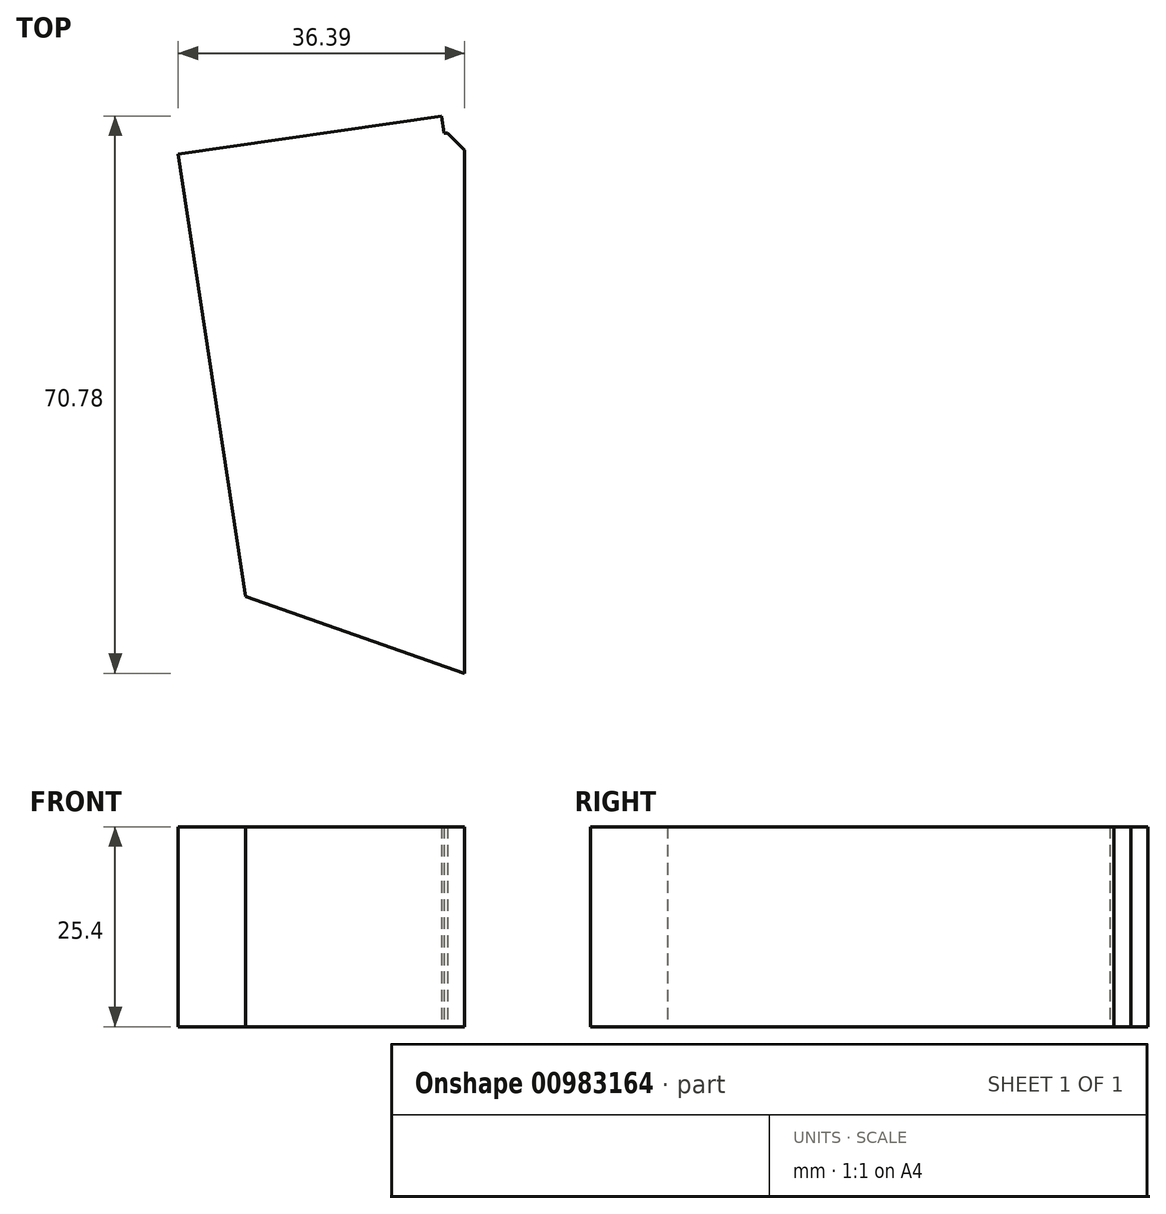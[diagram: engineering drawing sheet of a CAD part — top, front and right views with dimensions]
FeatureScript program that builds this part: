
annotation { "Feature Type Name" : "Feature", "Feature Type Description" : "" }
export const myFeature = defineFeature(function(context is Context, id is Id, definition is map)
    precondition{}
    {
        {
            var Q0;
            Q0=qCreatedBy(makeId("Top.planeOp"),FACE);
            var sketch = newSketch(context, id + "F0", { "sketchPlane" : qUnion([Q0])});
            skLineSegment(sketch, "E0", {"start": v(39.05, 32.74) * mm, "end": v(39.05, -33.74) * mm});
            skLineSegment(sketch, "E1", {"start": v(39.05, -33.74) * mm, "end": v(11.19, -24.02) * mm});
            skLineSegment(sketch, "E2", {"start": v(11.19, -24.02) * mm, "end": v(2.66, 32.2) * mm});
            skLineSegment(sketch, "E3", {"start": v(2.66, 32.2) * mm, "end": v(36.12, 37.04) * mm});
            skLineSegment(sketch, "E4", {"start": v(39.05, 32.74) * mm, "end": v(36.5, 35.2) * mm});
            skLineSegment(sketch, "E5", {"start": v(36.12, 37.04) * mm, "end": v(36.45, 34.86) * mm});
            skLineSegment(sketch, "E6", {"start": v(36.45, 34.86) * mm, "end": v(40.18, 34.86) * mm});
            skSolve(sketch);
        }
        {
            var Q0;
            Q0=qSketchRegion(id+"F0",true);
            extrude(context, id + "F1", {"entities" : qUnion([Q0]), "depth" : 25.4 * mm, "offsetDistance" : 25.4 * mm});
        }
    });
